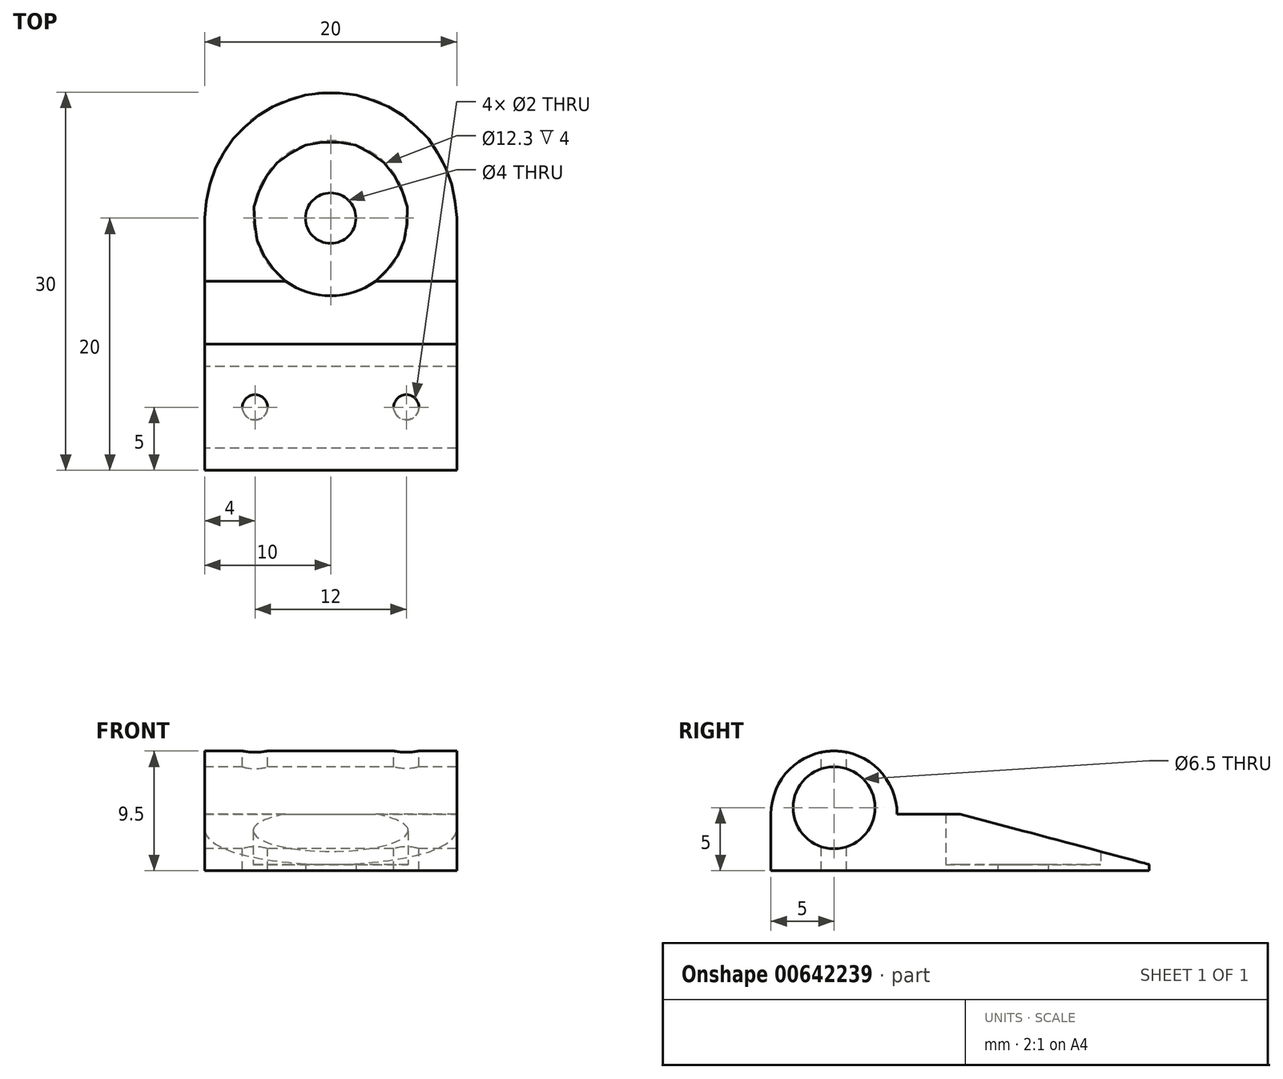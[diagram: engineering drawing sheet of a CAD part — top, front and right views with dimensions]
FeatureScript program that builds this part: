
annotation { "Feature Type Name" : "Feature", "Feature Type Description" : "" }
export const myFeature = defineFeature(function(context is Context, id is Id, definition is map)
    precondition{}
    {
        {
            var Q0;
            Q0=qCreatedBy(makeId("Top.planeOp"),FACE);
            var sketch = newSketch(context, id + "F0", { "sketchPlane" : qUnion([Q0])});
            skLineSegment(sketch, "E0.bottom", {"start": v(0, 0) * mm, "end": v(20, 0) * mm});
            skLineSegment(sketch, "E0.top", {"start": v(0, 30) * mm, "end": v(20, 30) * mm});
            skLineSegment(sketch, "E0.left", {"start": v(0, 0) * mm, "end": v(0, 30) * mm});
            skLineSegment(sketch, "E0.right", {"start": v(20, 0) * mm, "end": v(20, 30) * mm});
            skCircle(sketch, "E1", {"center": v(10, 20) * mm, "radius": 6.15 * mm});
            skCircle(sketch, "E2", {"center": v(10, 20) * mm, "radius": 2 * mm});
            skSolve(sketch);
        }
        {
            var Q0;
            Q0=makeQuery(id+"F0.imprint","IMPRINT",FACE,{"disambiguationData":[TD([[makeQuery(id+"F0.imprint","IMPRINT",EDGE,{"derivedFrom":sQuery(id+"F0.wireOp",EDGE,"E0.bottom")}),1.0]])]});
            extrude(context, id + "F1", {"entities" : qUnion([Q0]), "depth" : 4 * mm, "offsetDistance" : 25 * mm});
        }
        {
            var Q0;
            Q0=makeQuery(id+"F1.opExtrude","CAP_FACE",FACE,{"disambiguationData":[OSD([sQuery(id+"F0.wireOp",EDGE,"E0.bottom"),sQuery(id+"F0.wireOp",EDGE,"E0.top"),sQuery(id+"F0.wireOp",EDGE,"E0.left"),sQuery(id+"F0.wireOp",EDGE,"E0.right"),sQuery(id+"F0.wireOp",EDGE,"E1")])],"isStart":false});
            var Q1;
            Q1=makeQuery(id+"F0.imprint","IMPRINT",FACE,{"disambiguationData":[TD([[makeQuery(id+"F0.imprint","IMPRINT",EDGE,{"derivedFrom":sQuery(id+"F0.wireOp",EDGE,"E1")}),1.0]])]});
            var Q2;
            Q2=makeQuery(id+"F0.imprint","IMPRINT",FACE,{"disambiguationData":[TD([[makeQuery(id+"F0.imprint","IMPRINT",EDGE,{"derivedFrom":sQuery(id+"F0.wireOp",EDGE,"OT8LPEwu-qr0H-ovYg-CyCT-NBapPAweOkTc")}),1.0]])]});
            extrude(context, id + "F2", {"entities" : qUnion([Q0, Q1, Q2]), "operationType" : NewBodyOperationType.ADD, "depth" : 0.5 * mm, "offsetDistance" : 25 * mm});
        }
        {
            var Q0;
            Q0=makeQuery(id+"F2.opExtrude","CAP_FACE",FACE,{"disambiguationData":[OSD([sQuery(id+"F0.wireOp",EDGE,"E0.bottom"),sQuery(id+"F0.wireOp",EDGE,"E0.top"),sQuery(id+"F0.wireOp",EDGE,"E0.left"),sQuery(id+"F0.wireOp",EDGE,"E0.right"),sQuery(id+"F0.wireOp",EDGE,"E1")])],"isStart":false});
            var sketch = newSketch(context, id + "F3", { "sketchPlane" : qUnion([Q0])});
            skLineSegment(sketch, "E3.bottom", {"start": v(0, 0) * mm, "end": v(20, 0) * mm});
            skLineSegment(sketch, "E3.top", {"start": v(0, 10) * mm, "end": v(20, 10) * mm});
            skLineSegment(sketch, "E3.left", {"start": v(0, 0) * mm, "end": v(0, 10) * mm});
            skLineSegment(sketch, "E3.right", {"start": v(20, 0) * mm, "end": v(20, 10) * mm});
            skSolve(sketch);
        }
        {
            var Q0;
            Q0=makeQuery(id+"F3.imprint","IMPRINT",FACE,{"disambiguationData":[TD([[makeQuery(id+"F3.imprint","IMPRINT",EDGE,{"derivedFrom":sQuery(id+"F3.wireOp",EDGE,"E3.bottom")}),1.0]])]});
            extrude(context, id + "F4", {"entities" : qUnion([Q0]), "operationType" : NewBodyOperationType.ADD, "depth" : 5 * mm, "offsetDistance" : 25 * mm});
        }
        {
            var Q0;
            {var subQ0=sQuery(id+"F0.wireOp",EDGE,"E0.left");Q0=makeQuery(id+"F4.boolean.opBoolean","MERGE",FACE,{"derivedFrom":[makeQuery(id+"F2.boolean.opBoolean","MERGE",FACE,{"derivedFrom":[makeQuery(id+"F1.opExtrude","SWEPT_FACE",FACE,{"disambiguationData":[OSD([subQ0])]}),makeQuery(id+"F2.opExtrude","SWEPT_FACE",FACE,{"disambiguationData":[OSD([subQ0])]})]}),makeQuery(id+"F4.opExtrude","SWEPT_FACE",FACE,{"disambiguationData":[OSD([sQuery(id+"F3.wireOp",EDGE,"E3.left")])]})]});}
            var sketch = newSketch(context, id + "F5", { "sketchPlane" : qUnion([Q0])});
            skCircle(sketch, "E4", {"center": v(-5, 5) * mm, "radius": 3.25 * mm});
            skSolve(sketch);
        }
        {
            var Q0;
            Q0=makeQuery(id+"F5.imprint","IMPRINT",FACE,{"disambiguationData":[TD([[makeQuery(id+"F5.imprint","IMPRINT",EDGE,{"derivedFrom":sQuery(id+"F5.wireOp",EDGE,"E4")}),1.0]])]});
            extrude(context, id + "F6", {"entities" : qUnion([Q0]), "operationType" : NewBodyOperationType.REMOVE, "oppositeDirection" : true, "depth" : 25 * mm, "offsetDistance" : 25 * mm});
        }
        {
            var Q0;
            Q0=makeQuery(id+"F2.opExtrude","CAP_EDGE",EDGE,{"disambiguationData":[OSD([sQuery(id+"F0.wireOp",EDGE,"E0.top")])],"isStart":false});
            chamfer(context, id + "F7", {"entities" : qUnion([Q0]), "chamferType" : ChamferType.TWO_OFFSETS, "width1" : 4 * mm, "oppositeDirection" : false, "width2" : 15 * mm, "tangentPropagation" : true});
        }
        {
            var Q0;
            {var subQ0=sQuery(id+"F0.wireOp",EDGE,"E0.left");var subQ1=sQuery(id+"F0.wireOp",EDGE,"E0.top");Q0=makeQuery(id+"F2.boolean.opBoolean","MERGE",EDGE,{"derivedFrom":[makeQuery(id+"F1.opExtrude","SWEPT_EDGE",EDGE,{"disambiguationData":[OSD([subQ1,subQ0])]}),makeQuery(id+"F2.opExtrude","SWEPT_EDGE",EDGE,{"disambiguationData":[OSD([subQ1,subQ0])]})]});}
            var Q1;
            {var subQ0=sQuery(id+"F0.wireOp",EDGE,"E0.right");var subQ1=sQuery(id+"F0.wireOp",EDGE,"E0.top");Q1=makeQuery(id+"F2.boolean.opBoolean","MERGE",EDGE,{"derivedFrom":[makeQuery(id+"F1.opExtrude","SWEPT_EDGE",EDGE,{"disambiguationData":[OSD([subQ1,subQ0])]}),makeQuery(id+"F2.opExtrude","SWEPT_EDGE",EDGE,{"disambiguationData":[OSD([subQ1,subQ0])]})]});}
            fillet(context, id + "F8", {"entities" : qUnion([Q0, Q1]), "radius" : 10 * mm, "tangentPropagation" : true, "allowEdgeOverflow" : false});
        }
        {
            var Q0;
            Q0=makeQuery(id+"F4.opExtrude","CAP_FACE",FACE,{"disambiguationData":[OSD([sQuery(id+"F3.wireOp",EDGE,"E3.bottom"),sQuery(id+"F3.wireOp",EDGE,"E3.top"),sQuery(id+"F3.wireOp",EDGE,"E3.left"),sQuery(id+"F3.wireOp",EDGE,"E3.right")])],"isStart":false});
            var sketch = newSketch(context, id + "F9", { "sketchPlane" : qUnion([Q0])});
            skCircle(sketch, "E5", {"center": v(4, 5) * mm, "radius": 1 * mm});
            skCircle(sketch, "E6", {"center": v(16, 5) * mm, "radius": 1 * mm});
            skSolve(sketch);
        }
        {
            var Q0;
            Q0=makeQuery(id+"F9.imprint","IMPRINT",FACE,{"disambiguationData":[TD([[makeQuery(id+"F9.imprint","IMPRINT",EDGE,{"derivedFrom":sQuery(id+"F9.wireOp",EDGE,"E5")}),1.0]])]});
            var Q1;
            Q1=makeQuery(id+"F9.imprint","IMPRINT",FACE,{"disambiguationData":[TD([[makeQuery(id+"F9.imprint","IMPRINT",EDGE,{"derivedFrom":sQuery(id+"F9.wireOp",EDGE,"E6")}),1.0]])]});
            extrude(context, id + "F10", {"entities" : qUnion([Q0, Q1]), "operationType" : NewBodyOperationType.REMOVE, "oppositeDirection" : true, "depth" : 25 * mm, "offsetDistance" : 25 * mm});
        }
        {
            var Q0;
            Q0=makeQuery(id+"F4.opExtrude","CAP_EDGE",EDGE,{"disambiguationData":[OSD([sQuery(id+"F3.wireOp",EDGE,"E3.bottom")])],"isStart":false});
            var Q1;
            Q1=makeQuery(id+"F4.opExtrude","CAP_EDGE",EDGE,{"disambiguationData":[OSD([sQuery(id+"F3.wireOp",EDGE,"E3.top")])],"isStart":false});
            fillet(context, id + "F11", {"entities" : qUnion([Q0, Q1]), "radius" : 5 * mm, "tangentPropagation" : true, "allowEdgeOverflow" : false});
        }
    });
